# Revit family: 8000114 - Poppel with ashtray black free standing
name_source: partatom
category: Furniture
units: mm (PartAtom-declared; Revit-internal decimal feet)

## family parameters
Always vertical = Yes
Cut with Voids When Loaded = No
OmniClass Number = 23.11.27.00
Room Calculation Point = No
Shared = No
Work Plane-Based = No

## types (1)
- 8098592 Wooden Seat
    BIMobject category = Litter Bins
    Body material = Steel, Paint Finish, Black
    Construction material = Hags - Steel - Galvanized
    Default Elevation = 0 mm  [stored 0 ft]
    Description = Poppel with ashtray black free standing
    Edition number = 1
    IFC Classification = Object
    Manufacturer = Hags
    Manufacturer name = HAGS
    Model = 8000114
    OmniClass Code = 23-11 27 00
    OmniClass Description = Landscaping
    Product Guid = b9ca1c76-fcc6-4b73-bb62-e5fbca619f58
    Product name = Poppel with ashtray
    Product url = https://www.hags.com
    URL = https://www.hags.com
    Uniclass 1.4 Code = JN
    Uniclass 1.4 Description = Park Furniture/Equipment

note: [stored X ft] marks values corroborated as IEEE doubles in the binary element streams (Revit-internal decimal feet)

## geometry (parser evidence)
native form markers: Sweep x3
no freeform markers — native parametric forms only
